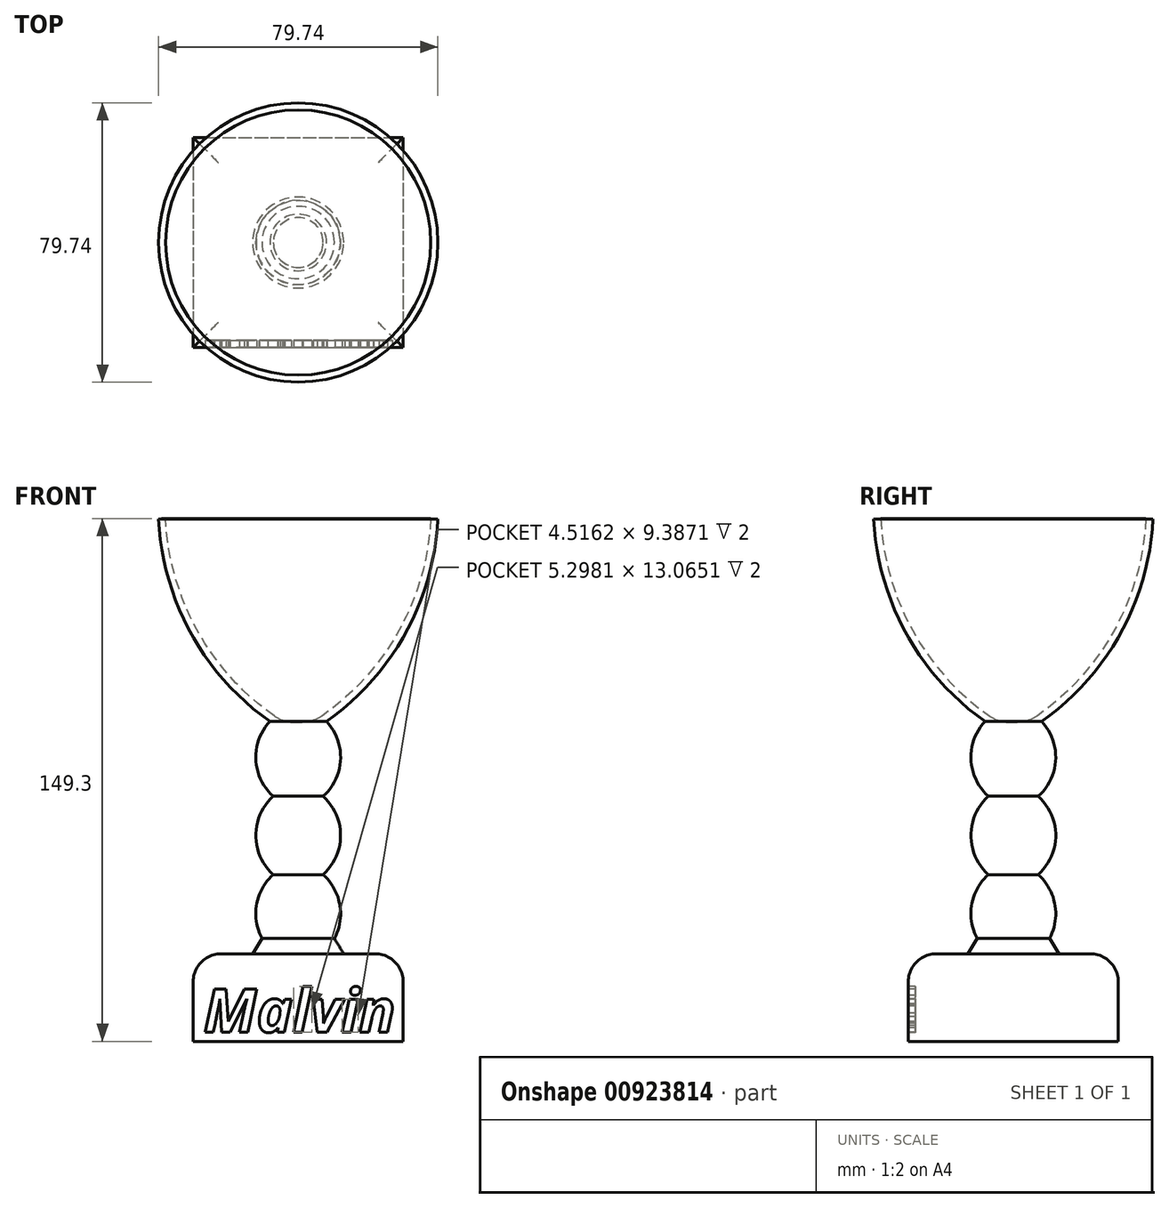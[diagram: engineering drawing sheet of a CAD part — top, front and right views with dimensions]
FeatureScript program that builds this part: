
annotation { "Feature Type Name" : "Feature", "Feature Type Description" : "" }
export const myFeature = defineFeature(function(context is Context, id is Id, definition is map)
    precondition{}
    {
        {
            var Q0;
            Q0=qCreatedBy(makeId("Top.planeOp"),FACE);
            var sketch = newSketch(context, id + "F0", { "sketchPlane" : qUnion([Q0])});
            skLineSegment(sketch, "E0.bottom", {"start": v(0, 0) * mm, "end": v(60, 0) * mm});
            skLineSegment(sketch, "E0.top", {"start": v(0, -60) * mm, "end": v(60, -60) * mm});
            skLineSegment(sketch, "E0.left", {"start": v(0, 0) * mm, "end": v(0, -60) * mm});
            skLineSegment(sketch, "E0.right", {"start": v(60, 0) * mm, "end": v(60, -60) * mm});
            skSolve(sketch);
        }
        {
            var Q0;
            Q0=makeQuery(id+"F0.imprint","IMPRINT",FACE,{"disambiguationData":[TD([[makeQuery(id+"F0.imprint","IMPRINT",EDGE,{"derivedFrom":sQuery(id+"F0.wireOp",EDGE,"E0.bottom")}),-1.0]])]});
            extrude(context, id + "F1", {"entities" : qUnion([Q0]), "depth" : 30 * mm, "offsetDistance" : 25 * mm});
        }
        {
            var Q0;
            Q0=makeQuery(id+"F1.opExtrude","SWEPT_BODY",BODY,{"disambiguationData":[OSD([sQuery(id+"F0.wireOp",EDGE,"E0.bottom"),sQuery(id+"F0.wireOp",EDGE,"E0.top"),sQuery(id+"F0.wireOp",EDGE,"E0.left"),sQuery(id+"F0.wireOp",EDGE,"E0.right")])]});
            transform(context, id + "F2", {"entities" : qUnion([Q0]), "transformType" : TransformType.TRANSLATION_3D, "dx" : -30 * mm, "dy" : 30 * mm, "dz" : 0 * mm, "makeCopy" : false});
        }
        {
            var Q0;
            Q0=qCreatedBy(makeId("Front.planeOp"),FACE);
            var sketch = newSketch(context, id + "F3", { "sketchPlane" : qUnion([Q0])});
            skArc(sketch, "E1", {"start": v(7.1, 30.27) * mm, "mid": v(12.1, 41.45) * mm, "end": v(7.1, 52.63) * mm});
            skArc(sketch, "E2", {"start": v(7.1, 52.63) * mm, "mid": v(12.1, 63.81) * mm, "end": v(7.1, 75) * mm});
            skArc(sketch, "E3", {"start": v(7.1, 75) * mm, "mid": v(12.1, 85.49) * mm, "end": v(8.09, 96.4) * mm});
            skLineSegment(sketch, "E4", {"start": v(0, 30.2) * mm, "end": v(0, 158.08) * mm});
            skLineSegment(sketch, "E5", {"start": v(7.1, 30.27) * mm, "end": v(7.1, 29.78) * mm});
            skLineSegment(sketch, "E6", {"start": v(7.1, 29.78) * mm, "end": v(0, 29.78) * mm});
            skLineSegment(sketch, "E7", {"start": v(0, 29.78) * mm, "end": v(0, 30.2) * mm});
            skArc(sketch, "E8", {"start": v(8.09, 96.4) * mm, "mid": v(30.66, 121.62) * mm, "end": v(39.87, 154.2) * mm});
            skLineSegment(sketch, "E9", {"start": v(37.87, 154.3) * mm, "end": v(39.87, 154.2) * mm});
            skLineSegment(sketch, "E10", {"start": v(0, 96.12) * mm, "end": v(1.06, 96.12) * mm});
            skArc(sketch, "E11.trimOffspring", {"start": v(6.8, 97.93) * mm, "mid": v(28.86, 122.52) * mm, "end": v(37.87, 154.3) * mm});
            skPoint(sketch, "E12.visualSharp", {"position": v(4.09, 96.12) * mm});
            skArc(sketch, "E12.filletArc", {"start": v(1.06, 96.12) * mm, "mid": v(4.07, 96.58) * mm, "end": v(6.8, 97.93) * mm});
            skSolve(sketch);
        }
        {
            var Q0;
            {var subQ10=sQuery(id+"F3.wireOp",EDGE,"I5DjJ9ts-EXyD-T3Ez-MTNL-TmspGHFE94tQ");Q0=makeQuery(id+"F3.imprint","IMPRINT",FACE,{"disambiguationData":[TD([[makeQuery(id+"F3.imprint","IMPRINT",EDGE,{"derivedFrom":subQ10}),1.0]])]});}
            var Q1;
            {var subQ0=sQuery(id+"F3.wireOp",EDGE,"E3");Q1=makeQuery(id+"F3.imprint","IMPRINT",FACE,{"disambiguationData":[TD([[makeQuery(id+"F3.imprint","IMPRINT",EDGE,{"derivedFrom":subQ0}),1.0]])]});}
            var Q2;
            {var subQ0=sQuery(id+"F3.wireOp",EDGE,"E2");Q2=makeQuery(id+"F3.imprint","IMPRINT",FACE,{"disambiguationData":[TD([[makeQuery(id+"F3.imprint","IMPRINT",EDGE,{"derivedFrom":subQ0}),1.0]])]});}
            var Q3;
            {var subQ0=sQuery(id+"F3.wireOp",EDGE,"E1");Q3=makeQuery(id+"F3.imprint","IMPRINT",FACE,{"disambiguationData":[TD([[makeQuery(id+"F3.imprint","IMPRINT",EDGE,{"derivedFrom":subQ0}),1.0]])]});}
            var Q4;
            Q4=sQuery(id+"F3.wireOp",EDGE,"E4");
            revolve(context, id + "F4", {"operationType" : NewBodyOperationType.ADD, "surfaceOperationType" : NewSurfaceOperationType.NEW, "entities" : qUnion([Q0, Q1, Q2, Q3]), "axis" : qUnion([Q4]), "revolveType" : RevolveType.FULL});
        }
        {
            var Q0;
            Q0=makeQuery(id+"F4.opRevolve","SWEPT_EDGE",EDGE,{"disambiguationData":[OSD([sQuery(id+"F3.wireOp",EDGE,"vcvWEaiL-wYzA-kxNN-2hgw-6SO7PC0KjmtI"),sQuery(id+"F3.wireOp",EDGE,"E1"),sQuery(id+"F3.wireOp",EDGE,"E5")])]});
            fillet(context, id + "F5", {"entities" : qUnion([Q0]), "radius" : 1 * mm, "tangentPropagation" : true, "allowEdgeOverflow" : false});
        }
        {
            var Q0;
            Q0=makeQuery(id+"F5.opFillet","BLEND_EDGE",EDGE,{"blendedFrom":[makeQuery(id+"F4.opRevolve","SWEPT_EDGE",EDGE,{"disambiguationData":[OSD([sQuery(id+"F3.wireOp",EDGE,"vcvWEaiL-wYzA-kxNN-2hgw-6SO7PC0KjmtI"),sQuery(id+"F3.wireOp",EDGE,"E1"),sQuery(id+"F3.wireOp",EDGE,"E5")])]}),makeQuery(id+"F1.opExtrude","CAP_FACE",FACE,{"disambiguationData":[OSD([sQuery(id+"F0.wireOp",EDGE,"E0.bottom"),sQuery(id+"F0.wireOp",EDGE,"E0.top"),sQuery(id+"F0.wireOp",EDGE,"E0.left"),sQuery(id+"F0.wireOp",EDGE,"E0.right")])],"isStart":false})],"blendedInto":[makeQuery(id+"F1.opExtrude","CAP_FACE",FACE,{"disambiguationData":[OSD([sQuery(id+"F0.wireOp",EDGE,"E0.bottom"),sQuery(id+"F0.wireOp",EDGE,"E0.top"),sQuery(id+"F0.wireOp",EDGE,"E0.left"),sQuery(id+"F0.wireOp",EDGE,"E0.right")])],"isStart":false})]});
            chamfer(context, id + "F6", {"entities" : qUnion([Q0]), "width" : 3 * mm, "tangentPropagation" : true});
        }
        {
            var Q0;
            Q0=makeQuery(id+"F1.opExtrude","CAP_EDGE",EDGE,{"disambiguationData":[OSD([sQuery(id+"F0.wireOp",EDGE,"E0.left")])],"isStart":false});
            var Q1;
            Q1=makeQuery(id+"F1.opExtrude","CAP_EDGE",EDGE,{"disambiguationData":[OSD([sQuery(id+"F0.wireOp",EDGE,"E0.bottom")])],"isStart":false});
            var Q2;
            Q2=makeQuery(id+"F1.opExtrude","CAP_EDGE",EDGE,{"disambiguationData":[OSD([sQuery(id+"F0.wireOp",EDGE,"E0.right")])],"isStart":false});
            var Q3;
            Q3=makeQuery(id+"F1.opExtrude","CAP_EDGE",EDGE,{"disambiguationData":[OSD([sQuery(id+"F0.wireOp",EDGE,"E0.top")])],"isStart":false});
            fillet(context, id + "F7", {"entities" : qUnion([Q0, Q1, Q2, Q3]), "radius" : 8 * mm, "tangentPropagation" : true, "allowEdgeOverflow" : false});
        }
        {
            var Q0;
            Q0=makeQuery(id+"F1.opExtrude","SWEPT_FACE",FACE,{"disambiguationData":[OSD([sQuery(id+"F0.wireOp",EDGE,"E0.top")])]});
            var sketch = newSketch(context, id + "F8", { "sketchPlane" : qUnion([Q0])});
            skText(sketch, "E13", { "text": "Malvin", "fontName": "OpenSans-BoldItalic.ttf"});
            const initialGuessF8  = {"E13": [-0.027, 0.00762, 1, 0, 0.01238]};
            skSetInitialGuess(sketch, initialGuessF8);
            skSolve(sketch);
        }
        {
            var Q0;
            Q0=qSketchRegion(id+"F8",true);
            extrude(context, id + "F9", {"entities" : qUnion([Q0]), "operationType" : NewBodyOperationType.REMOVE, "oppositeDirection" : true, "depth" : 2 * mm, "offsetDistance" : 25 * mm});
        }
        {
            var Q0;
            Q0=makeQuery(id+"F1.opExtrude","CAP_FACE",FACE,{"disambiguationData":[OSD([sQuery(id+"F0.wireOp",EDGE,"E0.bottom"),sQuery(id+"F0.wireOp",EDGE,"E0.top"),sQuery(id+"F0.wireOp",EDGE,"E0.left"),sQuery(id+"F0.wireOp",EDGE,"E0.right")])],"isStart":true});
            extrude(context, id + "F10", {"entities" : qUnion([Q0]), "operationType" : NewBodyOperationType.REMOVE, "oppositeDirection" : true, "depth" : 5 * mm, "offsetDistance" : 25 * mm});
        }
    });
